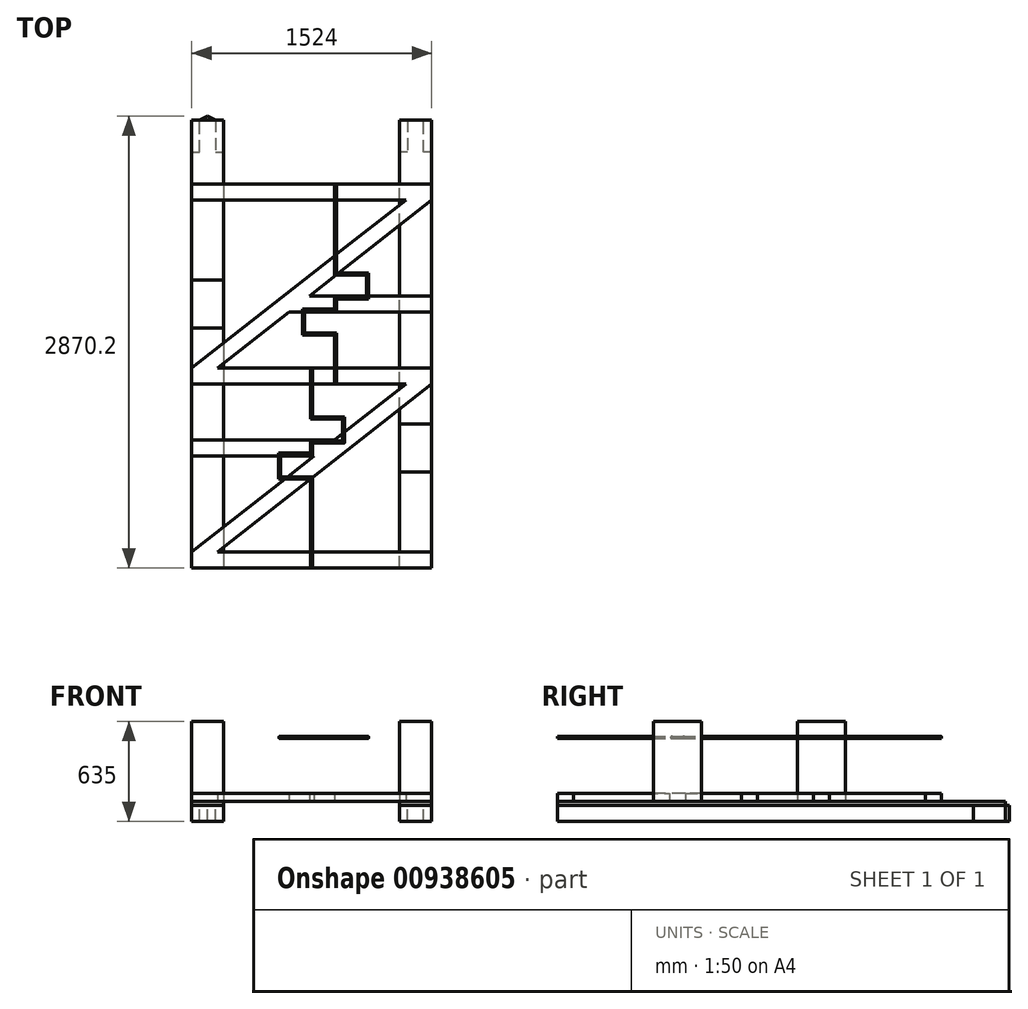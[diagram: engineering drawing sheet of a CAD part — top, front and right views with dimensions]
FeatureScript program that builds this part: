
annotation { "Feature Type Name" : "Feature", "Feature Type Description" : "" }
export const myFeature = defineFeature(function(context is Context, id is Id, definition is map)
    precondition{}
    {
        {
            var Q0;
            Q0=qCreatedBy(makeId("Top.planeOp"),FACE);
            cPlane(context, id + "F0", {"entities" : qUnion([Q0]), "cplaneType" : CPlaneType.OFFSET, "offset" : 406.4 * mm, "width" : 152.4 * mm, "height" : 152.4 * mm});
        }
        {
            var Q0;
            Q0=qCreatedBy(makeId("Top.planeOp"),FACE);
            var sketch = newSketch(context, id + "F1", { "sketchPlane" : qUnion([Q0])});
            skLineSegment(sketch, "E0.bottom", {"start": v(-762, 1219.2) * mm, "end": v(-558.8, 1219.2) * mm});
            skLineSegment(sketch, "E0.top", {"start": v(-762, -1219.2) * mm, "end": v(-558.8, -1219.2) * mm});
            skLineSegment(sketch, "E0.left", {"start": v(-762, 1219.2) * mm, "end": v(-762, -1219.2) * mm});
            skLineSegment(sketch, "E0.right", {"start": v(-558.8, 1219.2) * mm, "end": v(-558.8, -1219.2) * mm});
            skLineSegment(sketch, "E1.bottom", {"start": v(-558.8, -1219.2) * mm, "end": v(558.8, -1219.2) * mm});
            skLineSegment(sketch, "E1.top", {"start": v(-558.8, 1219.2) * mm, "end": v(558.8, 1219.2) * mm});
            skLineSegment(sketch, "E1.right", {"start": v(558.8, -1219.2) * mm, "end": v(558.8, 1219.2) * mm});
            skLineSegment(sketch, "E2.bottom", {"start": v(558.8, -1219.2) * mm, "end": v(762, -1219.2) * mm});
            skLineSegment(sketch, "E2.top", {"start": v(558.8, 1219.2) * mm, "end": v(762, 1219.2) * mm});
            skLineSegment(sketch, "E2.right", {"start": v(762, -1219.2) * mm, "end": v(762, 1219.2) * mm});
            skLineSegment(sketch, "E3", {"start": v(0, 1219.2) * mm, "end": v(0, -1219.2) * mm});
            skLineSegment(sketch, "E4", {"start": v(152.4, 1219.2) * mm, "end": v(152.4, -50.8) * mm});
            skPoint(sketch, "E5", {"position": v(0, 0) * mm});
            skLineSegment(sketch, "E6", {"start": v(152.4, 647.7) * mm, "end": v(355.6, 647.7) * mm});
            skLineSegment(sketch, "E7", {"start": v(355.6, 647.7) * mm, "end": v(355.6, 495.3) * mm});
            skLineSegment(sketch, "E8", {"start": v(355.6, 495.3) * mm, "end": v(152.4, 495.3) * mm});
            skPoint(sketch, "E9", {"position": v(152.4, 457.2) * mm});
            skPoint(sketch, "E10", {"position": v(355.6, 571.5) * mm});
            skLineSegment(sketch, "E11", {"start": v(152.4, 419.1) * mm, "end": v(-50.8, 419.1) * mm});
            skLineSegment(sketch, "E12", {"start": v(-50.8, 419.1) * mm, "end": v(-50.8, 266.7) * mm});
            skLineSegment(sketch, "E13", {"start": v(-50.8, 266.7) * mm, "end": v(152.4, 266.7) * mm});
            skPoint(sketch, "E14", {"position": v(-50.8, 342.9) * mm});
            skLineSegment(sketch, "E15", {"start": v(-762, 609.6) * mm, "end": v(-558.8, 609.6) * mm});
            skLineSegment(sketch, "E16", {"start": v(-762, 304.8) * mm, "end": v(-558.8, 304.8) * mm});
            skPoint(sketch, "E17", {"position": v(-558.8, 457.2) * mm});
            skLineSegment(sketch, "E18", {"start": v(762, -304.8) * mm, "end": v(558.8, -304.8) * mm});
            skLineSegment(sketch, "E19", {"start": v(558.8, -304.8) * mm, "end": v(558.8, -609.6) * mm});
            skLineSegment(sketch, "E20", {"start": v(558.8, -609.6) * mm, "end": v(762, -609.6) * mm});
            skPoint(sketch, "E21", {"position": v(558.8, -457.2) * mm});
            skLineSegment(sketch, "E22", {"start": v(-762, 1219.2) * mm, "end": v(-762, 1422.4) * mm});
            skLineSegment(sketch, "E23", {"start": v(-762, 1422.4) * mm, "end": v(-558.8, 1422.4) * mm});
            skLineSegment(sketch, "E24", {"start": v(-558.8, 1422.4) * mm, "end": v(-558.8, 1219.2) * mm});
            skLineSegment(sketch, "E25", {"start": v(-660.4, 1422.4) * mm, "end": v(-660.4, 1219.2) * mm});
            skLineSegment(sketch, "E26", {"start": v(-711.2, 1422.4) * mm, "end": v(-711.2, 1625.6) * mm});
            skLineSegment(sketch, "E27", {"start": v(-711.2, 1625.6) * mm, "end": v(-609.6, 1625.6) * mm});
            skLineSegment(sketch, "E28", {"start": v(-609.6, 1625.6) * mm, "end": v(-609.6, 1422.4) * mm});
            skLineSegment(sketch, "E29", {"start": v(-711.2, 1625.6) * mm, "end": v(-660.4, 1651) * mm});
            skLineSegment(sketch, "E30", {"start": v(-660.4, 1651) * mm, "end": v(-609.6, 1625.6) * mm});
            skLineSegment(sketch, "E31", {"start": v(-660.4, 1625.6) * mm, "end": v(-660.4, 1651) * mm, "construction": true});
            skLineSegment(sketch, "E32.MirrorCS", {"start": v(711.2, 1625.6) * mm, "end": v(609.6, 1625.6) * mm});
            skLineSegment(sketch, "E33.MirrorCS", {"start": v(660.4, 1625.6) * mm, "end": v(660.4, 1651) * mm, "construction": true});
            skLineSegment(sketch, "E34.MirrorCS", {"start": v(660.4, 1651) * mm, "end": v(609.6, 1625.6) * mm});
            skLineSegment(sketch, "E35.MirrorCS", {"start": v(711.2, 1625.6) * mm, "end": v(660.4, 1651) * mm});
            skLineSegment(sketch, "E36.MirrorCS", {"start": v(762, 1422.4) * mm, "end": v(558.8, 1422.4) * mm});
            skLineSegment(sketch, "E37.MirrorCS", {"start": v(609.6, 1625.6) * mm, "end": v(609.6, 1422.4) * mm});
            skLineSegment(sketch, "E38.MirrorCS", {"start": v(711.2, 1422.4) * mm, "end": v(711.2, 1625.6) * mm});
            skLineSegment(sketch, "E39.MirrorCS", {"start": v(558.8, 1422.4) * mm, "end": v(558.8, 1219.2) * mm});
            skLineSegment(sketch, "E40.MirrorCS", {"start": v(762, 1219.2) * mm, "end": v(762, 1422.4) * mm});
            skLineSegment(sketch, "E41.MirrorCS", {"start": v(660.4, 1422.4) * mm, "end": v(660.4, 1219.2) * mm});
            skLineSegment(sketch, "E42", {"start": v(-762, 1422.4) * mm, "end": v(-762, 1625.6) * mm});
            skLineSegment(sketch, "E43", {"start": v(-762, 1625.6) * mm, "end": v(-558.8, 1625.6) * mm});
            skLineSegment(sketch, "E44", {"start": v(-558.8, 1625.6) * mm, "end": v(-558.8, 1422.4) * mm});
            skLineSegment(sketch, "E45.MirrorCS", {"start": v(558.8, 1625.6) * mm, "end": v(558.8, 1422.4) * mm});
            skLineSegment(sketch, "E46.MirrorCS", {"start": v(762, 1422.4) * mm, "end": v(762, 1625.6) * mm});
            skLineSegment(sketch, "E47.MirrorCS", {"start": v(762, 1625.6) * mm, "end": v(558.8, 1625.6) * mm});
            skSolve(sketch);
        }
        {
            var Q0;
            {var subQ3=sQuery(id+"F1.wireOp",EDGE,"E15");Q0=makeQuery(id+"F1.imprint","IMPRINT",FACE,{"disambiguationData":[TD([[makeQuery(id+"F1.imprint","IMPRINT",EDGE,{"derivedFrom":subQ3}),1.0]])]});}
            var Q1;
            {var subQ0=sQuery(id+"F1.wireOp",EDGE,"E15");Q1=makeQuery(id+"F1.imprint","IMPRINT",FACE,{"disambiguationData":[TD([[makeQuery(id+"F1.imprint","IMPRINT",EDGE,{"derivedFrom":subQ0}),-1.0]])]});}
            var Q2;
            {var subQ0=sQuery(id+"F1.wireOp",EDGE,"E0.top");Q2=makeQuery(id+"F1.imprint","IMPRINT",FACE,{"disambiguationData":[TD([[makeQuery(id+"F1.imprint","IMPRINT",EDGE,{"derivedFrom":subQ0}),1.0]])]});}
            var Q3;
            {var subQ0=sQuery(id+"F1.wireOp",EDGE,"E2.bottom");Q3=makeQuery(id+"F1.imprint","IMPRINT",FACE,{"disambiguationData":[TD([[makeQuery(id+"F1.imprint","IMPRINT",EDGE,{"derivedFrom":subQ0}),1.0]])]});}
            var Q4;
            {var subQ3=sQuery(id+"F1.wireOp",EDGE,"E18");Q4=makeQuery(id+"F1.imprint","IMPRINT",FACE,{"disambiguationData":[TD([[makeQuery(id+"F1.imprint","IMPRINT",EDGE,{"derivedFrom":subQ3}),-1.0]])]});}
            var Q5;
            {var subQ0=sQuery(id+"F1.wireOp",EDGE,"E18");Q5=makeQuery(id+"F1.imprint","IMPRINT",FACE,{"disambiguationData":[TD([[makeQuery(id+"F1.imprint","IMPRINT",EDGE,{"derivedFrom":subQ0}),1.0]])]});}
            var Q6;
            {var subQ1=sQuery(id+"F1.wireOp",EDGE,"E26");Q6=makeQuery(id+"F1.imprint","IMPRINT",FACE,{"disambiguationData":[TD([[makeQuery(id+"F1.imprint","IMPRINT",EDGE,{"derivedFrom":subQ1}),-1.0]])]});}
            var Q7;
            {var subQ0=sQuery(id+"F1.wireOp",EDGE,"E29");Q7=makeQuery(id+"F1.imprint","IMPRINT",FACE,{"disambiguationData":[TD([[makeQuery(id+"F1.imprint","IMPRINT",EDGE,{"derivedFrom":subQ0}),-1.0]])]});}
            var Q8;
            {var subQ0=sQuery(id+"F1.wireOp",EDGE,"E30");Q8=makeQuery(id+"F1.imprint","IMPRINT",FACE,{"disambiguationData":[TD([[makeQuery(id+"F1.imprint","IMPRINT",EDGE,{"derivedFrom":subQ0}),-1.0]])]});}
            var Q9;
            {var subQ0=sQuery(id+"F1.wireOp",EDGE,"E24");Q9=makeQuery(id+"F1.imprint","IMPRINT",FACE,{"disambiguationData":[TD([[makeQuery(id+"F1.imprint","IMPRINT",EDGE,{"derivedFrom":subQ0}),-1.0]])]});}
            var Q10;
            {var subQ3=sQuery(id+"F1.wireOp",EDGE,"E22");Q10=makeQuery(id+"F1.imprint","IMPRINT",FACE,{"disambiguationData":[TD([[makeQuery(id+"F1.imprint","IMPRINT",EDGE,{"derivedFrom":subQ3}),-1.0]])]});}
            var Q11;
            {var subQ0=sQuery(id+"F1.wireOp",EDGE,"E40.MirrorCS");Q11=makeQuery(id+"F1.imprint","IMPRINT",FACE,{"disambiguationData":[TD([[makeQuery(id+"F1.imprint","IMPRINT",EDGE,{"derivedFrom":subQ0}),1.0]])]});}
            var Q12;
            {var subQ0=sQuery(id+"F1.wireOp",EDGE,"E37.MirrorCS");Q12=makeQuery(id+"F1.imprint","IMPRINT",FACE,{"disambiguationData":[TD([[makeQuery(id+"F1.imprint","IMPRINT",EDGE,{"derivedFrom":subQ0}),1.0]])]});}
            var Q13;
            {var subQ0=sQuery(id+"F1.wireOp",EDGE,"E39.MirrorCS");Q13=makeQuery(id+"F1.imprint","IMPRINT",FACE,{"disambiguationData":[TD([[makeQuery(id+"F1.imprint","IMPRINT",EDGE,{"derivedFrom":subQ0}),1.0]])]});}
            var Q14;
            {var subQ2=sQuery(id+"F1.wireOp",EDGE,"E33.MirrorCS");Q14=makeQuery(id+"F1.imprint","IMPRINT",FACE,{"disambiguationData":[TD([[makeQuery(id+"F1.imprint","IMPRINT",EDGE,{"derivedFrom":subQ2}),1.0]])]});}
            var Q15;
            {var subQ2=sQuery(id+"F1.wireOp",EDGE,"E33.MirrorCS");Q15=makeQuery(id+"F1.imprint","IMPRINT",FACE,{"disambiguationData":[TD([[makeQuery(id+"F1.imprint","IMPRINT",EDGE,{"derivedFrom":subQ2}),-1.0]])]});}
            extrude(context, id + "F2", {"entities" : qUnion([Q0, Q1, Q2, Q3, Q4, Q5, Q6, Q7, Q8, Q9, Q10, Q11, Q12, Q13, Q14, Q15]), "oppositeDirection" : true, "depth" : 127 * mm, "offsetDistance" : 25.4 * mm, "hasSecondDirection" : true, "secondDirectionOppositeDirection" : true, "secondDirectionDepth" : 25.4 * mm});
        }
        {
            var Q0;
            {var subQ0=sQuery(id+"F1.wireOp",EDGE,"E15");Q0=makeQuery(id+"F1.imprint","IMPRINT",FACE,{"disambiguationData":[TD([[makeQuery(id+"F1.imprint","IMPRINT",EDGE,{"derivedFrom":subQ0}),-1.0]])]});}
            extrude(context, id + "F3", {"entities" : qUnion([Q0]), "depth" : 508 * mm, "offsetDistance" : 25.4 * mm});
        }
        {
            var Q0;
            {var subQ0=sQuery(id+"F1.wireOp",EDGE,"E18");Q0=makeQuery(id+"F1.imprint","IMPRINT",FACE,{"disambiguationData":[TD([[makeQuery(id+"F1.imprint","IMPRINT",EDGE,{"derivedFrom":subQ0}),1.0]])]});}
            extrude(context, id + "F4", {"entities" : qUnion([Q0]), "depth" : 508 * mm, "offsetDistance" : 25.4 * mm});
        }
        {
            var Q0;
            Q0=qCreatedBy(id+"F0.planeOp",FACE);
            var sketch = newSketch(context, id + "F5", { "sketchPlane" : qUnion([Q0])});
            skLineSegment(sketch, "E48.0", {"start": v(0, 50.8) * mm, "end": v(0, -266.7) * mm});
            skLineSegment(sketch, "E49", {"start": v(0, -266.7) * mm, "end": v(203.2, -266.7) * mm});
            skLineSegment(sketch, "E50", {"start": v(203.2, -266.7) * mm, "end": v(203.2, -419.1) * mm});
            skLineSegment(sketch, "E51", {"start": v(203.2, -419.1) * mm, "end": v(0, -419.1) * mm});
            skLineSegment(sketch, "E52", {"start": v(0, -495.3) * mm, "end": v(-203.2, -495.3) * mm});
            skLineSegment(sketch, "E53", {"start": v(-203.2, -495.3) * mm, "end": v(-203.2, -647.7) * mm});
            skLineSegment(sketch, "E54", {"start": v(-203.2, -647.7) * mm, "end": v(0, -647.7) * mm});
            skPoint(sketch, "E55", {"position": v(0, -457.2) * mm});
            skPoint(sketch, "E56", {"position": v(203.2, -342.9) * mm});
            skPoint(sketch, "E57", {"position": v(-203.2, -571.5) * mm});
            skPoint(sketch, "E58.orphan", {"position": v(0, 1219.2) * mm});
            skLineSegment(sketch, "E59.0", {"start": v(152.4, 1219.2) * mm, "end": v(152.4, 647.7) * mm});
            skLineSegment(sketch, "E59.1", {"start": v(152.4, 647.7) * mm, "end": v(355.6, 647.7) * mm});
            skLineSegment(sketch, "E59.2", {"start": v(355.6, 495.3) * mm, "end": v(152.4, 495.3) * mm});
            skLineSegment(sketch, "E59.3", {"start": v(355.6, 647.7) * mm, "end": v(355.6, 495.3) * mm});
            skLineSegment(sketch, "E59.4", {"start": v(152.4, 419.1) * mm, "end": v(-50.8, 419.1) * mm});
            skLineSegment(sketch, "E59.5", {"start": v(-50.8, 419.1) * mm, "end": v(-50.8, 266.7) * mm});
            skLineSegment(sketch, "E59.6", {"start": v(-50.8, 266.7) * mm, "end": v(152.4, 266.7) * mm});
            skLineSegment(sketch, "E60", {"start": v(146.05, 1219.2) * mm, "end": v(146.05, 641.35) * mm});
            skLineSegment(sketch, "E61", {"start": v(146.05, 641.35) * mm, "end": v(349.25, 641.35) * mm});
            skLineSegment(sketch, "E62", {"start": v(349.25, 641.35) * mm, "end": v(349.25, 501.65) * mm});
            skLineSegment(sketch, "E63", {"start": v(349.25, 501.65) * mm, "end": v(146.05, 501.65) * mm});
            skLineSegment(sketch, "E64", {"start": v(146.05, 501.65) * mm, "end": v(146.05, 425.45) * mm});
            skLineSegment(sketch, "E65", {"start": v(146.05, 425.45) * mm, "end": v(-57.15, 425.45) * mm});
            skLineSegment(sketch, "E66", {"start": v(-57.15, 425.45) * mm, "end": v(-57.15, 260.35) * mm});
            skLineSegment(sketch, "E67", {"start": v(-57.15, 260.35) * mm, "end": v(146.05, 260.35) * mm});
            skLineSegment(sketch, "E68", {"start": v(146.05, 260.35) * mm, "end": v(146.05, -50.8) * mm});
            skLineSegment(sketch, "E69", {"start": v(158.75, 1219.2) * mm, "end": v(158.75, 654.05) * mm});
            skLineSegment(sketch, "E70", {"start": v(158.75, 654.05) * mm, "end": v(361.95, 654.05) * mm});
            skLineSegment(sketch, "E71", {"start": v(361.95, 654.05) * mm, "end": v(361.95, 488.95) * mm});
            skLineSegment(sketch, "E72", {"start": v(361.95, 488.95) * mm, "end": v(158.75, 488.95) * mm});
            skLineSegment(sketch, "E73", {"start": v(158.75, 488.95) * mm, "end": v(158.75, 412.75) * mm});
            skLineSegment(sketch, "E74", {"start": v(158.75, 412.75) * mm, "end": v(-44.45, 412.75) * mm});
            skLineSegment(sketch, "E75", {"start": v(-44.45, 412.75) * mm, "end": v(-44.45, 273.05) * mm});
            skLineSegment(sketch, "E76", {"start": v(-44.45, 273.05) * mm, "end": v(158.75, 273.05) * mm});
            skLineSegment(sketch, "E77", {"start": v(158.75, 273.05) * mm, "end": v(158.75, -50.8) * mm});
            skLineSegment(sketch, "E78", {"start": v(146.05, -50.8) * mm, "end": v(158.75, -50.8) * mm});
            skLineSegment(sketch, "E79", {"start": v(146.05, 1219.2) * mm, "end": v(158.75, 1219.2) * mm});
            skLineSegment(sketch, "E80.trimOffspring", {"start": v(152.4, 495.3) * mm, "end": v(152.4, 419.1) * mm});
            skLineSegment(sketch, "E81.trimOffspring", {"start": v(152.4, 266.7) * mm, "end": v(152.4, -50.8) * mm});
            skLineSegment(sketch, "E82.trimOffspring", {"start": v(0, -419.1) * mm, "end": v(0, -495.3) * mm});
            skLineSegment(sketch, "E83.trimOffspring", {"start": v(0, -647.7) * mm, "end": v(0, -1219.2) * mm});
            skSolve(sketch);
        }
        {
            var Q0;
            {var subQ2=sQuery(id+"F1.wireOp",EDGE,"E26");Q0=makeQuery(id+"F1.imprint","IMPRINT",FACE,{"disambiguationData":[TD([[makeQuery(id+"F1.imprint","IMPRINT",EDGE,{"derivedFrom":subQ2}),1.0]])]});}
            var Q1;
            {var subQ3=sQuery(id+"F1.wireOp",EDGE,"E26");Q1=makeQuery(id+"F1.imprint","IMPRINT",FACE,{"disambiguationData":[TD([[makeQuery(id+"F1.imprint","IMPRINT",EDGE,{"derivedFrom":subQ3}),-1.0]])]});}
            var Q2;
            {var subQ2=sQuery(id+"F1.wireOp",EDGE,"E28");Q2=makeQuery(id+"F1.imprint","IMPRINT",FACE,{"disambiguationData":[TD([[makeQuery(id+"F1.imprint","IMPRINT",EDGE,{"derivedFrom":subQ2}),1.0]])]});}
            var Q3;
            {var subQ0=sQuery(id+"F1.wireOp",EDGE,"E24");Q3=makeQuery(id+"F1.imprint","IMPRINT",FACE,{"disambiguationData":[TD([[makeQuery(id+"F1.imprint","IMPRINT",EDGE,{"derivedFrom":subQ0}),-1.0]])]});}
            var Q4;
            {var subQ3=sQuery(id+"F1.wireOp",EDGE,"E22");Q4=makeQuery(id+"F1.imprint","IMPRINT",FACE,{"disambiguationData":[TD([[makeQuery(id+"F1.imprint","IMPRINT",EDGE,{"derivedFrom":subQ3}),-1.0]])]});}
            var Q5;
            {var subQ3=sQuery(id+"F1.wireOp",EDGE,"E15");Q5=makeQuery(id+"F1.imprint","IMPRINT",FACE,{"disambiguationData":[TD([[makeQuery(id+"F1.imprint","IMPRINT",EDGE,{"derivedFrom":subQ3}),1.0]])]});}
            var Q6;
            {var subQ0=sQuery(id+"F1.wireOp",EDGE,"E0.top");Q6=makeQuery(id+"F1.imprint","IMPRINT",FACE,{"disambiguationData":[TD([[makeQuery(id+"F1.imprint","IMPRINT",EDGE,{"derivedFrom":subQ0}),1.0]])]});}
            var Q7;
            {var subQ3=sQuery(id+"F1.wireOp",EDGE,"E18");Q7=makeQuery(id+"F1.imprint","IMPRINT",FACE,{"disambiguationData":[TD([[makeQuery(id+"F1.imprint","IMPRINT",EDGE,{"derivedFrom":subQ3}),-1.0]])]});}
            var Q8;
            {var subQ0=sQuery(id+"F1.wireOp",EDGE,"E2.bottom");Q8=makeQuery(id+"F1.imprint","IMPRINT",FACE,{"disambiguationData":[TD([[makeQuery(id+"F1.imprint","IMPRINT",EDGE,{"derivedFrom":subQ0}),1.0]])]});}
            var Q9;
            {var subQ2=sQuery(id+"F1.wireOp",EDGE,"E37.MirrorCS");Q9=makeQuery(id+"F1.imprint","IMPRINT",FACE,{"disambiguationData":[TD([[makeQuery(id+"F1.imprint","IMPRINT",EDGE,{"derivedFrom":subQ2}),-1.0]])]});}
            var Q10;
            {var subQ1=sQuery(id+"F1.wireOp",EDGE,"E37.MirrorCS");Q10=makeQuery(id+"F1.imprint","IMPRINT",FACE,{"disambiguationData":[TD([[makeQuery(id+"F1.imprint","IMPRINT",EDGE,{"derivedFrom":subQ1}),1.0]])]});}
            var Q11;
            {var subQ2=sQuery(id+"F1.wireOp",EDGE,"E38.MirrorCS");Q11=makeQuery(id+"F1.imprint","IMPRINT",FACE,{"disambiguationData":[TD([[makeQuery(id+"F1.imprint","IMPRINT",EDGE,{"derivedFrom":subQ2}),-1.0]])]});}
            var Q12;
            {var subQ0=sQuery(id+"F1.wireOp",EDGE,"E40.MirrorCS");Q12=makeQuery(id+"F1.imprint","IMPRINT",FACE,{"disambiguationData":[TD([[makeQuery(id+"F1.imprint","IMPRINT",EDGE,{"derivedFrom":subQ0}),1.0]])]});}
            var Q13;
            {var subQ0=sQuery(id+"F1.wireOp",EDGE,"E39.MirrorCS");Q13=makeQuery(id+"F1.imprint","IMPRINT",FACE,{"disambiguationData":[TD([[makeQuery(id+"F1.imprint","IMPRINT",EDGE,{"derivedFrom":subQ0}),1.0]])]});}
            var Q14;
            {var subQ0=sQuery(id+"F1.wireOp",EDGE,"E15");Q14=makeQuery(id+"F1.imprint","IMPRINT",FACE,{"disambiguationData":[TD([[makeQuery(id+"F1.imprint","IMPRINT",EDGE,{"derivedFrom":subQ0}),-1.0]])]});}
            var Q15;
            {var subQ0=sQuery(id+"F1.wireOp",EDGE,"E18");Q15=makeQuery(id+"F1.imprint","IMPRINT",FACE,{"disambiguationData":[TD([[makeQuery(id+"F1.imprint","IMPRINT",EDGE,{"derivedFrom":subQ0}),1.0]])]});}
            extrude(context, id + "F6", {"entities" : qUnion([Q0, Q1, Q2, Q3, Q4, Q5, Q6, Q7, Q8, Q9, Q10, Q11, Q12, Q13, Q14, Q15]), "oppositeDirection" : true, "depth" : 25.4 * mm, "offsetDistance" : 25.4 * mm});
        }
        {
            var Q0;
            Q0=qCreatedBy(makeId("Top.planeOp"),FACE);
            var sketch = newSketch(context, id + "F7", { "sketchPlane" : qUnion([Q0])});
            skLineSegment(sketch, "E84.0", {"start": v(-762, 1219.2) * mm, "end": v(-762, -1219.2) * mm});
            skLineSegment(sketch, "E84.1", {"start": v(-558.8, 1219.2) * mm, "end": v(-558.8, -1219.2) * mm});
            skLineSegment(sketch, "E84.2", {"start": v(558.8, -1219.2) * mm, "end": v(558.8, 1219.2) * mm});
            skLineSegment(sketch, "E84.3", {"start": v(762, -1219.2) * mm, "end": v(762, 1219.2) * mm});
            skLineSegment(sketch, "E85.0", {"start": v(-558.8, 1219.2) * mm, "end": v(558.8, 1219.2) * mm});
            skLineSegment(sketch, "E85.1", {"start": v(-762, 1219.2) * mm, "end": v(-558.8, 1219.2) * mm});
            skLineSegment(sketch, "E85.2", {"start": v(558.8, 1219.2) * mm, "end": v(762, 1219.2) * mm});
            skLineSegment(sketch, "E85.3", {"start": v(0, 1219.2) * mm, "end": v(0, -1219.2) * mm});
            skLineSegment(sketch, "E85.4", {"start": v(-558.8, -1219.2) * mm, "end": v(558.8, -1219.2) * mm});
            skLineSegment(sketch, "E85.5", {"start": v(-762, -1219.2) * mm, "end": v(-558.8, -1219.2) * mm});
            skLineSegment(sketch, "E85.6", {"start": v(558.8, -1219.2) * mm, "end": v(762, -1219.2) * mm});
            skLineSegment(sketch, "E86", {"start": v(-762, 1117.6) * mm, "end": v(762, 1117.6) * mm});
            skLineSegment(sketch, "E87", {"start": v(-762, -1117.6) * mm, "end": v(762, -1117.6) * mm});
            skLineSegment(sketch, "E88", {"start": v(-762, 0) * mm, "end": v(762, 0) * mm, "construction": true});
            skLineSegment(sketch, "E89", {"start": v(-762, 50.8) * mm, "end": v(762, 50.8) * mm});
            skLineSegment(sketch, "E90.MirrorCS", {"start": v(-762, -50.8) * mm, "end": v(762, -50.8) * mm});
            skLineSegment(sketch, "E91", {"start": v(-762, -1117.6) * mm, "end": v(597.43, -50.8) * mm});
            skLineSegment(sketch, "E92", {"start": v(762, -50.8) * mm, "end": v(-597.43, -1117.6) * mm});
            skLineSegment(sketch, "E93", {"start": v(597.43, 1117.6) * mm, "end": v(-762, 50.8) * mm});
            skLineSegment(sketch, "E94", {"start": v(-597.43, 50.8) * mm, "end": v(762, 1117.6) * mm});
            skLineSegment(sketch, "E95", {"start": v(-14.81, 508) * mm, "end": v(762, 508) * mm});
            skLineSegment(sketch, "E96", {"start": v(762, 406.4) * mm, "end": v(-144.28, 406.4) * mm});
            skLineSegment(sketch, "E97", {"start": v(762, 457.2) * mm, "end": v(-79.55, 457.2) * mm, "construction": true});
            skLineSegment(sketch, "E98", {"start": v(-762, -406.4) * mm, "end": v(144.28, -406.4) * mm});
            skLineSegment(sketch, "E99", {"start": v(14.81, -508) * mm, "end": v(-762, -508) * mm});
            skLineSegment(sketch, "E100", {"start": v(-762, -457.2) * mm, "end": v(79.55, -457.2) * mm, "construction": true});
            skSolve(sketch);
        }
        {
            var Q0;
            {var subQ0=sQuery(id+"F7.wireOp",EDGE,"E93");var subQ1=sQuery(id+"F7.wireOp",EDGE,"E84.1");var subQ2=makeQuery(id+"F7.imprint","INTERSECT",VERTEX,{"derivedFrom":[subQ1,subQ0]});Q0=makeQuery(id+"F7.imprint","IMPRINT",FACE,{"disambiguationData":[TD([[makeQuery(id+"F7.imprint","IMPRINT",EDGE,{"disambiguationData":[TD([[subQ2,-1.0]])],"derivedFrom":subQ1}),1.0]])]});}
            var Q1;
            {var subQ0=sQuery(id+"F7.wireOp",EDGE,"E93");var subQ1=sQuery(id+"F7.wireOp",EDGE,"E84.1");var subQ2=makeQuery(id+"F7.imprint","INTERSECT",VERTEX,{"derivedFrom":[subQ1,subQ0]});Q1=makeQuery(id+"F7.imprint","IMPRINT",FACE,{"disambiguationData":[TD([[makeQuery(id+"F7.imprint","IMPRINT",EDGE,{"disambiguationData":[TD([[subQ2,-1.0]])],"derivedFrom":subQ1}),-1.0]])]});}
            var Q2;
            {var subQ0=sQuery(id+"F7.wireOp",EDGE,"E94");var subQ1=sQuery(id+"F7.wireOp",EDGE,"E84.2");var subQ2=makeQuery(id+"F7.imprint","INTERSECT",VERTEX,{"derivedFrom":[subQ1,subQ0]});Q2=makeQuery(id+"F7.imprint","IMPRINT",FACE,{"disambiguationData":[TD([[makeQuery(id+"F7.imprint","IMPRINT",EDGE,{"disambiguationData":[TD([[subQ2,-1.0]])],"derivedFrom":subQ1}),1.0]])]});}
            var Q3;
            {var subQ0=sQuery(id+"F7.wireOp",EDGE,"E94");var subQ1=sQuery(id+"F7.wireOp",EDGE,"E84.2");var subQ2=makeQuery(id+"F7.imprint","INTERSECT",VERTEX,{"derivedFrom":[subQ1,subQ0]});Q3=makeQuery(id+"F7.imprint","IMPRINT",FACE,{"disambiguationData":[TD([[makeQuery(id+"F7.imprint","IMPRINT",EDGE,{"disambiguationData":[TD([[subQ2,-1.0]])],"derivedFrom":subQ1}),-1.0]])]});}
            var Q4;
            {var subQ4=sQuery(id+"F7.wireOp",EDGE,"E85.2");Q4=makeQuery(id+"F7.imprint","IMPRINT",FACE,{"disambiguationData":[TD([[makeQuery(id+"F7.imprint","IMPRINT",EDGE,{"derivedFrom":subQ4}),-1.0]])]});}
            var Q5;
            {var subQ0=sQuery(id+"F7.wireOp",EDGE,"E85.0");var subQ5=sQuery(id+"F7.wireOp",EDGE,"E85.3");var subQ6=makeQuery(id+"F7.imprint","INTERSECT",VERTEX,{"derivedFrom":[subQ0,subQ5]});Q5=makeQuery(id+"F7.imprint","IMPRINT",FACE,{"disambiguationData":[TD([[makeQuery(id+"F7.imprint","IMPRINT",EDGE,{"disambiguationData":[TD([[subQ6,-1.0]])],"derivedFrom":subQ5}),1.0]])]});}
            var Q6;
            {var subQ0=sQuery(id+"F7.wireOp",EDGE,"E85.0");var subQ5=sQuery(id+"F7.wireOp",EDGE,"E85.3");var subQ6=makeQuery(id+"F7.imprint","INTERSECT",VERTEX,{"derivedFrom":[subQ0,subQ5]});Q6=makeQuery(id+"F7.imprint","IMPRINT",FACE,{"disambiguationData":[TD([[makeQuery(id+"F7.imprint","IMPRINT",EDGE,{"disambiguationData":[TD([[subQ6,-1.0]])],"derivedFrom":subQ5}),-1.0]])]});}
            var Q7;
            {var subQ0=sQuery(id+"F7.wireOp",EDGE,"E85.1");Q7=makeQuery(id+"F7.imprint","IMPRINT",FACE,{"disambiguationData":[TD([[makeQuery(id+"F7.imprint","IMPRINT",EDGE,{"derivedFrom":subQ0}),-1.0]])]});}
            var Q8;
            {var subQ0=sQuery(id+"F7.wireOp",EDGE,"E89");var subQ1=sQuery(id+"F7.wireOp",EDGE,"E84.1");var subQ2=makeQuery(id+"F7.imprint","INTERSECT",VERTEX,{"derivedFrom":[subQ1,subQ0]});Q8=makeQuery(id+"F7.imprint","IMPRINT",FACE,{"disambiguationData":[TD([[makeQuery(id+"F7.imprint","IMPRINT",EDGE,{"disambiguationData":[TD([[subQ2,-1.0]])],"derivedFrom":subQ1}),1.0]])]});}
            var Q9;
            {var subQ0=sQuery(id+"F7.wireOp",EDGE,"E89");var subQ2=sQuery(id+"F7.wireOp",EDGE,"E84.1");var subQ3=makeQuery(id+"F7.imprint","INTERSECT",VERTEX,{"derivedFrom":[subQ2,subQ0]});Q9=makeQuery(id+"F7.imprint","IMPRINT",FACE,{"disambiguationData":[TD([[makeQuery(id+"F7.imprint","IMPRINT",EDGE,{"disambiguationData":[TD([[subQ3,-1.0]])],"derivedFrom":subQ2}),-1.0]])]});}
            var Q10;
            {var subQ0=sQuery(id+"F7.wireOp",EDGE,"E90.MirrorCS");var subQ1=sQuery(id+"F7.wireOp",EDGE,"E84.2");var subQ2=makeQuery(id+"F7.imprint","INTERSECT",VERTEX,{"derivedFrom":[subQ1,subQ0]});Q10=makeQuery(id+"F7.imprint","IMPRINT",FACE,{"disambiguationData":[TD([[makeQuery(id+"F7.imprint","IMPRINT",EDGE,{"disambiguationData":[TD([[subQ2,-1.0]])],"derivedFrom":subQ1}),1.0]])]});}
            var Q11;
            {var subQ3=sQuery(id+"F7.wireOp",EDGE,"E84.2");var subQ5=sQuery(id+"F7.wireOp",EDGE,"E90.MirrorCS");var subQ8=makeQuery(id+"F7.imprint","INTERSECT",VERTEX,{"derivedFrom":[subQ3,subQ5]});Q11=makeQuery(id+"F7.imprint","IMPRINT",FACE,{"disambiguationData":[TD([[makeQuery(id+"F7.imprint","IMPRINT",EDGE,{"disambiguationData":[TD([[subQ8,-1.0]])],"derivedFrom":subQ3}),-1.0]])]});}
            var Q12;
            {var subQ0=sQuery(id+"F7.wireOp",EDGE,"E92");var subQ1=sQuery(id+"F7.wireOp",EDGE,"E84.2");var subQ2=makeQuery(id+"F7.imprint","INTERSECT",VERTEX,{"derivedFrom":[subQ1,subQ0]});Q12=makeQuery(id+"F7.imprint","IMPRINT",FACE,{"disambiguationData":[TD([[makeQuery(id+"F7.imprint","IMPRINT",EDGE,{"disambiguationData":[TD([[subQ2,-1.0]])],"derivedFrom":subQ1}),1.0]])]});}
            var Q13;
            {var subQ0=sQuery(id+"F7.wireOp",EDGE,"E92");var subQ1=sQuery(id+"F7.wireOp",EDGE,"E84.2");var subQ2=makeQuery(id+"F7.imprint","INTERSECT",VERTEX,{"derivedFrom":[subQ1,subQ0]});Q13=makeQuery(id+"F7.imprint","IMPRINT",FACE,{"disambiguationData":[TD([[makeQuery(id+"F7.imprint","IMPRINT",EDGE,{"disambiguationData":[TD([[subQ2,-1.0]])],"derivedFrom":subQ1}),-1.0]])]});}
            var Q14;
            {var subQ0=sQuery(id+"F7.wireOp",EDGE,"E91");var subQ1=sQuery(id+"F7.wireOp",EDGE,"E84.1");var subQ2=makeQuery(id+"F7.imprint","INTERSECT",VERTEX,{"derivedFrom":[subQ1,subQ0]});Q14=makeQuery(id+"F7.imprint","IMPRINT",FACE,{"disambiguationData":[TD([[makeQuery(id+"F7.imprint","IMPRINT",EDGE,{"disambiguationData":[TD([[subQ2,-1.0]])],"derivedFrom":subQ1}),1.0]])]});}
            var Q15;
            {var subQ0=sQuery(id+"F7.wireOp",EDGE,"E91");var subQ1=sQuery(id+"F7.wireOp",EDGE,"E84.1");var subQ2=makeQuery(id+"F7.imprint","INTERSECT",VERTEX,{"derivedFrom":[subQ1,subQ0]});Q15=makeQuery(id+"F7.imprint","IMPRINT",FACE,{"disambiguationData":[TD([[makeQuery(id+"F7.imprint","IMPRINT",EDGE,{"disambiguationData":[TD([[subQ2,-1.0]])],"derivedFrom":subQ1}),-1.0]])]});}
            var Q16;
            {var subQ0=sQuery(id+"F7.wireOp",EDGE,"E85.4");var subQ5=sQuery(id+"F7.wireOp",EDGE,"E85.3");var subQ6=makeQuery(id+"F7.imprint","INTERSECT",VERTEX,{"derivedFrom":[subQ5,subQ0]});Q16=makeQuery(id+"F7.imprint","IMPRINT",FACE,{"disambiguationData":[TD([[makeQuery(id+"F7.imprint","IMPRINT",EDGE,{"disambiguationData":[TD([[subQ6,1.0]])],"derivedFrom":subQ5}),-1.0]])]});}
            var Q17;
            {var subQ4=sQuery(id+"F7.wireOp",EDGE,"E85.5");Q17=makeQuery(id+"F7.imprint","IMPRINT",FACE,{"disambiguationData":[TD([[makeQuery(id+"F7.imprint","IMPRINT",EDGE,{"derivedFrom":subQ4}),1.0]])]});}
            var Q18;
            {var subQ0=sQuery(id+"F7.wireOp",EDGE,"E85.4");var subQ5=sQuery(id+"F7.wireOp",EDGE,"E85.3");var subQ6=makeQuery(id+"F7.imprint","INTERSECT",VERTEX,{"derivedFrom":[subQ5,subQ0]});Q18=makeQuery(id+"F7.imprint","IMPRINT",FACE,{"disambiguationData":[TD([[makeQuery(id+"F7.imprint","IMPRINT",EDGE,{"disambiguationData":[TD([[subQ6,1.0]])],"derivedFrom":subQ5}),1.0]])]});}
            var Q19;
            {var subQ0=sQuery(id+"F7.wireOp",EDGE,"E85.6");Q19=makeQuery(id+"F7.imprint","IMPRINT",FACE,{"disambiguationData":[TD([[makeQuery(id+"F7.imprint","IMPRINT",EDGE,{"derivedFrom":subQ0}),1.0]])]});}
            var Q20;
            {var subQ0=sQuery(id+"F7.wireOp",EDGE,"E98");var subQ1=sQuery(id+"F7.wireOp",EDGE,"E84.1");var subQ2=makeQuery(id+"F7.imprint","INTERSECT",VERTEX,{"derivedFrom":[subQ1,subQ0]});Q20=makeQuery(id+"F7.imprint","IMPRINT",FACE,{"disambiguationData":[TD([[makeQuery(id+"F7.imprint","IMPRINT",EDGE,{"disambiguationData":[TD([[subQ2,-1.0]])],"derivedFrom":subQ1}),1.0]])]});}
            var Q21;
            {var subQ0=sQuery(id+"F7.wireOp",EDGE,"E98");var subQ1=sQuery(id+"F7.wireOp",EDGE,"E84.0");var subQ2=makeQuery(id+"F7.imprint","INTERSECT",VERTEX,{"derivedFrom":[subQ1,subQ0]});Q21=makeQuery(id+"F7.imprint","IMPRINT",FACE,{"disambiguationData":[TD([[makeQuery(id+"F7.imprint","IMPRINT",EDGE,{"disambiguationData":[TD([[subQ2,-1.0]])],"derivedFrom":subQ1}),1.0]])]});}
            var Q22;
            {var subQ0=sQuery(id+"F7.wireOp",EDGE,"E98");var subQ1=sQuery(id+"F7.wireOp",EDGE,"E85.3");var subQ2=makeQuery(id+"F7.imprint","INTERSECT",VERTEX,{"derivedFrom":[subQ1,subQ0]});Q22=makeQuery(id+"F7.imprint","IMPRINT",FACE,{"disambiguationData":[TD([[makeQuery(id+"F7.imprint","IMPRINT",EDGE,{"disambiguationData":[TD([[subQ2,-1.0]])],"derivedFrom":subQ1}),1.0]])]});}
            var Q23;
            {var subQ0=sQuery(id+"F7.wireOp",EDGE,"E95");var subQ1=sQuery(id+"F7.wireOp",EDGE,"E85.3");var subQ2=makeQuery(id+"F7.imprint","INTERSECT",VERTEX,{"derivedFrom":[subQ1,subQ0]});Q23=makeQuery(id+"F7.imprint","IMPRINT",FACE,{"disambiguationData":[TD([[makeQuery(id+"F7.imprint","IMPRINT",EDGE,{"disambiguationData":[TD([[subQ2,-1.0]])],"derivedFrom":subQ1}),-1.0]])]});}
            var Q24;
            {var subQ0=sQuery(id+"F7.wireOp",EDGE,"E96");var subQ1=sQuery(id+"F7.wireOp",EDGE,"E84.2");var subQ2=makeQuery(id+"F7.imprint","INTERSECT",VERTEX,{"derivedFrom":[subQ1,subQ0]});Q24=makeQuery(id+"F7.imprint","IMPRINT",FACE,{"disambiguationData":[TD([[makeQuery(id+"F7.imprint","IMPRINT",EDGE,{"disambiguationData":[TD([[subQ2,-1.0]])],"derivedFrom":subQ1}),-1.0]])]});}
            var Q25;
            {var subQ0=sQuery(id+"F7.wireOp",EDGE,"E96");var subQ1=sQuery(id+"F7.wireOp",EDGE,"E84.2");var subQ2=makeQuery(id+"F7.imprint","INTERSECT",VERTEX,{"derivedFrom":[subQ1,subQ0]});Q25=makeQuery(id+"F7.imprint","IMPRINT",FACE,{"disambiguationData":[TD([[makeQuery(id+"F7.imprint","IMPRINT",EDGE,{"disambiguationData":[TD([[subQ2,-1.0]])],"derivedFrom":subQ1}),1.0]])]});}
            extrude(context, id + "F8", {"entities" : qUnion([Q0, Q1, Q2, Q3, Q4, Q5, Q6, Q7, Q8, Q9, Q10, Q11, Q12, Q13, Q14, Q15, Q16, Q17, Q18, Q19, Q20, Q21, Q22, Q23, Q24, Q25]), "depth" : 50.8 * mm, "offsetDistance" : 25.4 * mm});
        }
        {
            var Q0;
            Q0=makeQuery(id+"F8.opExtrude","CAP_FACE",FACE,{"disambiguationData":[OSD([sQuery(id+"F7.wireOp",EDGE,"E84.0"),sQuery(id+"F7.wireOp",EDGE,"E84.3"),sQuery(id+"F7.wireOp",EDGE,"E85.0"),sQuery(id+"F7.wireOp",EDGE,"E85.1"),sQuery(id+"F7.wireOp",EDGE,"E85.2"),sQuery(id+"F7.wireOp",EDGE,"E85.4"),sQuery(id+"F7.wireOp",EDGE,"E85.5"),sQuery(id+"F7.wireOp",EDGE,"E85.6"),sQuery(id+"F7.wireOp",EDGE,"E86"),sQuery(id+"F7.wireOp",EDGE,"E87"),sQuery(id+"F7.wireOp",EDGE,"E89"),sQuery(id+"F7.wireOp",EDGE,"E90.MirrorCS"),sQuery(id+"F7.wireOp",EDGE,"E91"),sQuery(id+"F7.wireOp",EDGE,"E92"),sQuery(id+"F7.wireOp",EDGE,"E93"),sQuery(id+"F7.wireOp",EDGE,"E94"),sQuery(id+"F7.wireOp",EDGE,"E95"),sQuery(id+"F7.wireOp",EDGE,"E96"),sQuery(id+"F7.wireOp",EDGE,"E98"),sQuery(id+"F7.wireOp",EDGE,"E99")])],"isStart":false});
            cPlane(context, id + "F9", {"entities" : qUnion([Q0]), "cplaneType" : CPlaneType.OFFSET, "offset" : 0 * mm, "width" : 152.4 * mm, "height" : 152.4 * mm});
        }
        {
            var Q0;
            Q0=makeQuery(id+"F8.opExtrude","SWEPT_FACE",FACE,{"disambiguationData":[OSD([sQuery(id+"F7.wireOp",EDGE,"E85.4"),sQuery(id+"F7.wireOp",EDGE,"E85.5"),sQuery(id+"F7.wireOp",EDGE,"E85.6")])]});
            cPlane(context, id + "F10", {"entities" : qUnion([Q0]), "cplaneType" : CPlaneType.OFFSET, "offset" : 0 * mm, "width" : 152.4 * mm, "height" : 152.4 * mm});
        }
        {
            var Q0;
            Q0=makeQuery(id+"F8.opExtrude","SWEPT_FACE",FACE,{"disambiguationData":[OSD([sQuery(id+"F7.wireOp",EDGE,"E85.0"),sQuery(id+"F7.wireOp",EDGE,"E85.1"),sQuery(id+"F7.wireOp",EDGE,"E85.2")])]});
            cPlane(context, id + "F11", {"entities" : qUnion([Q0]), "cplaneType" : CPlaneType.OFFSET, "offset" : 0 * mm, "width" : 152.4 * mm, "height" : 152.4 * mm});
        }
        {
            var Q0;
            Q0=qCreatedBy(id+"F11.planeOp",FACE);
            var sketch = newSketch(context, id + "F12", { "sketchPlane" : qUnion([Q0])});
            skPoint(sketch, "E101.0", {"position": v(-152.4, 406.4) * mm});
            skPoint(sketch, "E101.1", {"position": v(-158.75, 406.4) * mm});
            skCircle(sketch, "E102", {"center": v(-152.4, 406.4) * mm, "radius": 6.35 * mm});
            skSolve(sketch);
        }
        {
            var Q0;
            Q0=makeQuery(id+"F12.imprint","IMPRINT",FACE,{"disambiguationData":[TD([[makeQuery(id+"F12.imprint","IMPRINT",EDGE,{"derivedFrom":sQuery(id+"F12.wireOp",EDGE,"E102")}),1.0]])]});
            var Q1;
            Q1=sQuery(id+"F5.wireOp",EDGE,"E59.0");
            var Q2;
            Q2=sQuery(id+"F5.wireOp",EDGE,"E59.1");
            var Q3;
            Q3=sQuery(id+"F5.wireOp",EDGE,"E59.3");
            var Q4;
            Q4=sQuery(id+"F5.wireOp",EDGE,"E59.2");
            var Q5;
            Q5=sQuery(id+"F5.wireOp",EDGE,"E80.trimOffspring");
            var Q6;
            Q6=sQuery(id+"F5.wireOp",EDGE,"E59.4");
            var Q7;
            Q7=sQuery(id+"F5.wireOp",EDGE,"E59.5");
            var Q8;
            Q8=sQuery(id+"F5.wireOp",EDGE,"E81.trimOffspring");
            var Q9;
            Q9=sQuery(id+"F5.wireOp",EDGE,"E59.6");
            sweep(context, id + "F13", {"profiles" : qUnion([Q0]), "path" : qUnion([Q1, Q2, Q3, Q4, Q5, Q6, Q7, Q8, Q9])});
        }
        {
            var Q0;
            Q0=qCreatedBy(id+"F10.planeOp",FACE);
            var sketch = newSketch(context, id + "F14", { "sketchPlane" : qUnion([Q0])});
            skPoint(sketch, "E103.0", {"position": v(0, 406.4) * mm});
            skCircle(sketch, "E104", {"center": v(0, 406.4) * mm, "radius": 6.35 * mm});
            skSolve(sketch);
        }
        {
            var Q0;
            Q0=makeQuery(id+"F14.imprint","IMPRINT",FACE,{"disambiguationData":[TD([[makeQuery(id+"F14.imprint","IMPRINT",EDGE,{"derivedFrom":sQuery(id+"F14.wireOp",EDGE,"E104")}),1.0]])]});
            var Q1;
            Q1=sQuery(id+"F5.wireOp",EDGE,"E83.trimOffspring");
            var Q2;
            Q2=sQuery(id+"F5.wireOp",EDGE,"E48.0");
            var Q3;
            Q3=sQuery(id+"F5.wireOp",EDGE,"E49");
            var Q4;
            Q4=sQuery(id+"F5.wireOp",EDGE,"E50");
            var Q5;
            Q5=sQuery(id+"F5.wireOp",EDGE,"E51");
            var Q6;
            Q6=sQuery(id+"F5.wireOp",EDGE,"E82.trimOffspring");
            var Q7;
            Q7=sQuery(id+"F5.wireOp",EDGE,"E52");
            var Q8;
            Q8=sQuery(id+"F5.wireOp",EDGE,"E53");
            var Q9;
            Q9=sQuery(id+"F5.wireOp",EDGE,"E54");
            sweep(context, id + "F15", {"profiles" : qUnion([Q0]), "path" : qUnion([Q1, Q2, Q3, Q4, Q5, Q6, Q7, Q8, Q9])});
        }
    });
